# Revit family: Plumbing-Soap-Dispensers-Sloan-Valve-ESD-200
name_source: partatom
category: Specialty Equipment
units: mm (PartAtom-declared; Revit-internal decimal feet)

## family parameters
Cut with Voids When Loaded = No
Host = Face
OmniClass Number = 23.40.20.21.34
Part Type = Normal
Room Calculation Point = No
Round Connector Dimension = Use Diameter
Shared = No

## types (2) — shared parameters
Apparent Load = 216 VA
Assembly Code = D2010
CW Connection = Yes
Connector Description = Electrical Connection
Current = 2 A
Depth = 5.38 "
Edition number = 1
HW Connection = Yes
Height = 4.25 "
Keynote = 15410
Manufacturer = Sloan Valve
Model = ESD-200-LT-CP
Number of Poles = 1
Power Factor = 1
Product Material = Sloan Valve - Finish - Polished Chrome
URL = www.sloanvalve.com
Vent Connection = No
Voltage = 120 V
Waste Connection = No
Width = 1.8 "
zero-valued in all types: Default Elevation

## per-type parameters (varying)
| type | Description | Part Number |
| ESD-200-LT-CP | Optima® Deck-Mounted Liquid Soap Dispenser, Less (specify separately) Transformer, Polished Chrome Finish | 3346052 |
| ESD-200-PLG-CP | Optima® Deck-Mounted Liquid Soap Dispenser, Plug-In Transformer, Polished Chrome Finish | 3346051 |

## geometry (parser evidence)
native form markers: Sweep x7
no freeform markers — native parametric forms only
